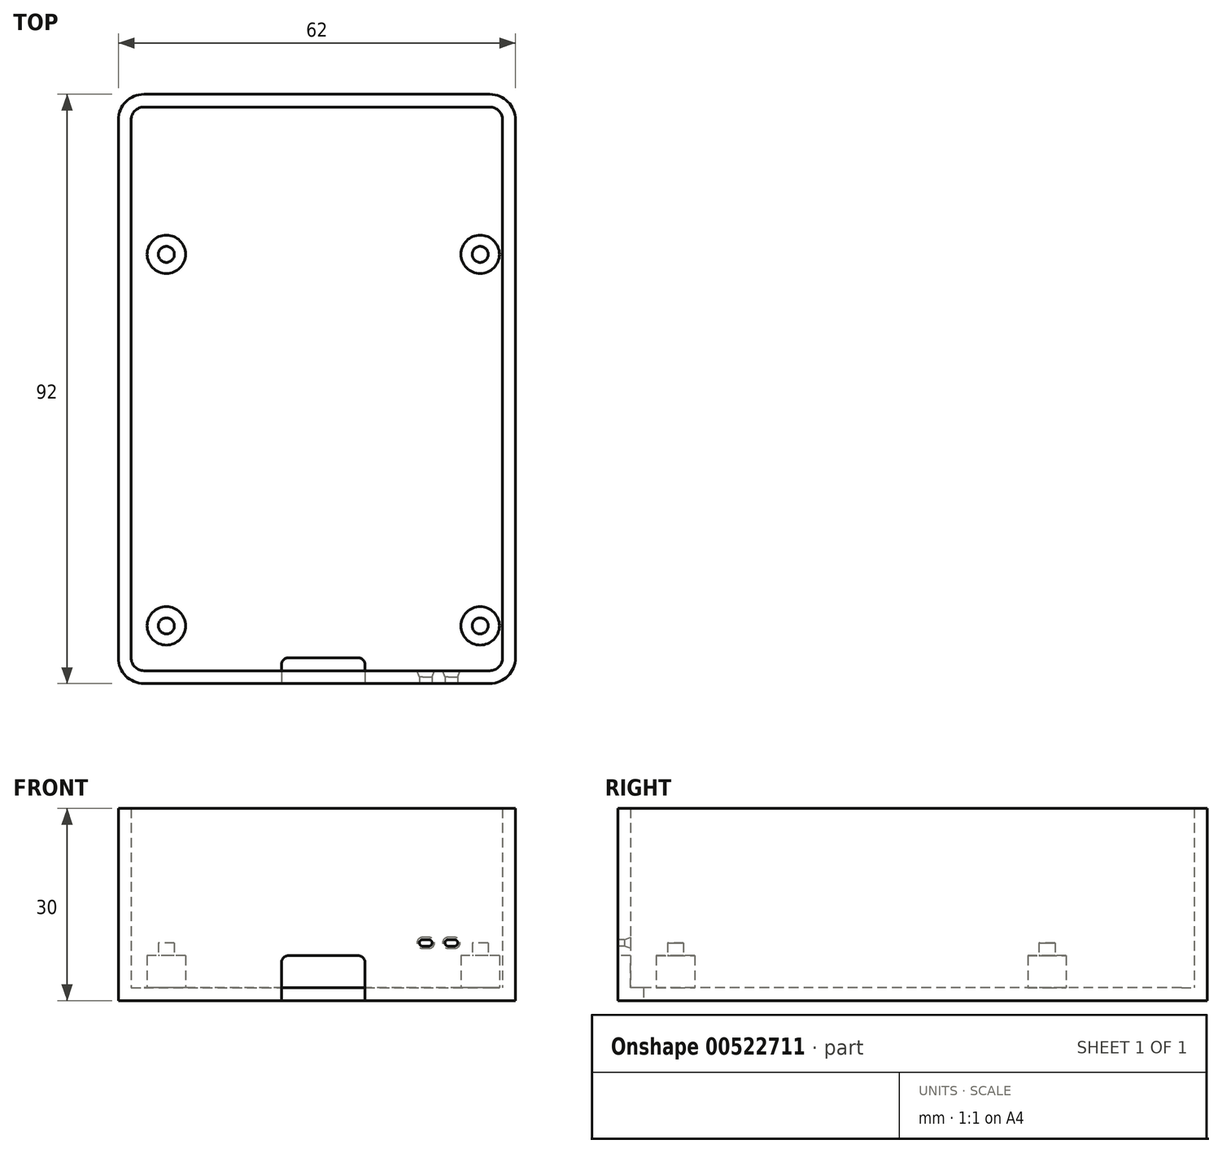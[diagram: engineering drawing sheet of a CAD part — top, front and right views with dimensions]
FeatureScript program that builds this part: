
annotation { "Feature Type Name" : "Feature", "Feature Type Description" : "" }
export const myFeature = defineFeature(function(context is Context, id is Id, definition is map)
    precondition{}
    {
        {
            var Q0;
            Q0=qCreatedBy(makeId("Top.planeOp"),FACE);
            var sketch = newSketch(context, id + "F0", { "sketchPlane" : qUnion([Q0])});
            skLineSegment(sketch, "E0.bottom", {"start": v(62, 0) * mm, "end": v(0, 0) * mm});
            skLineSegment(sketch, "E0.top", {"start": v(62, 92) * mm, "end": v(0, 92) * mm});
            skLineSegment(sketch, "E0.left", {"start": v(62, 0) * mm, "end": v(62, 92) * mm});
            skLineSegment(sketch, "E0.right", {"start": v(0, 0) * mm, "end": v(0, 92) * mm});
            skSolve(sketch);
        }
        {
            var Q0;
            Q0=makeQuery(id+"F0.imprint","IMPRINT",FACE,{"disambiguationData":[TD([[makeQuery(id+"F0.imprint","IMPRINT",EDGE,{"derivedFrom":sQuery(id+"F0.wireOp",EDGE,"E0.bottom")}),-1.0]])]});
            extrude(context, id + "F1", {"entities" : qUnion([Q0]), "depth" : 2 * mm});
        }
        {
            var Q0;
            Q0=makeQuery(id+"F1.opExtrude","CAP_FACE",FACE,{"disambiguationData":[OSD([sQuery(id+"F0.wireOp",EDGE,"E0.bottom"),sQuery(id+"F0.wireOp",EDGE,"E0.top"),sQuery(id+"F0.wireOp",EDGE,"E0.left"),sQuery(id+"F0.wireOp",EDGE,"E0.right")])],"isStart":false});
            var sketch = newSketch(context, id + "F2", { "sketchPlane" : qUnion([Q0])});
            skLineSegment(sketch, "E1.0", {"start": v(2, 2) * mm, "end": v(60, 2) * mm});
            skLineSegment(sketch, "E1.1", {"start": v(2, 90) * mm, "end": v(2, 2) * mm});
            skLineSegment(sketch, "E1.2", {"start": v(60, 90) * mm, "end": v(2, 90) * mm});
            skLineSegment(sketch, "E1.3", {"start": v(60, 2) * mm, "end": v(60, 90) * mm});
            skLineSegment(sketch, "E2.bottom", {"start": v(7.5, 67) * mm, "end": v(56.5, 67) * mm, "construction": true});
            skLineSegment(sketch, "E2.top", {"start": v(7.5, 9) * mm, "end": v(56.5, 9) * mm, "construction": true});
            skLineSegment(sketch, "E2.left", {"start": v(7.5, 67) * mm, "end": v(7.5, 9) * mm, "construction": true});
            skLineSegment(sketch, "E2.right", {"start": v(56.5, 67) * mm, "end": v(56.5, 9) * mm, "construction": true});
            skCircle(sketch, "E3", {"center": v(7.5, 67) * mm, "radius": 3 * mm});
            skCircle(sketch, "E4", {"center": v(56.5, 67) * mm, "radius": 3 * mm});
            skCircle(sketch, "E5", {"center": v(56.5, 9) * mm, "radius": 3 * mm});
            skCircle(sketch, "E6", {"center": v(7.5, 9) * mm, "radius": 3 * mm});
            skSolve(sketch);
        }
        {
            var Q0;
            Q0=makeQuery(id+"F2.imprint","IMPRINT",FACE,{"disambiguationData":[TD([[makeQuery(id+"F2.imprint","IMPRINT",EDGE,{"derivedFrom":sQuery(id+"F2.wireOp",EDGE,"E1.0")}),-1.0]])]});
            var Q1;
            Q1=makeQuery(id+"F2.imprint","IMPRINT",FACE,{"disambiguationData":[TD([[makeQuery(id+"F2.imprint","IMPRINT",EDGE,{"derivedFrom":sQuery(id+"F2.wireOp",EDGE,"E3")}),1.0]])]});
            var Q2;
            Q2=makeQuery(id+"F2.imprint","IMPRINT",FACE,{"disambiguationData":[TD([[makeQuery(id+"F2.imprint","IMPRINT",EDGE,{"derivedFrom":sQuery(id+"F2.wireOp",EDGE,"E4")}),1.0]])]});
            var Q3;
            Q3=makeQuery(id+"F2.imprint","IMPRINT",FACE,{"disambiguationData":[TD([[makeQuery(id+"F2.imprint","IMPRINT",EDGE,{"derivedFrom":sQuery(id+"F2.wireOp",EDGE,"E6")}),1.0]])]});
            var Q4;
            Q4=makeQuery(id+"F2.imprint","IMPRINT",FACE,{"disambiguationData":[TD([[makeQuery(id+"F2.imprint","IMPRINT",EDGE,{"derivedFrom":sQuery(id+"F2.wireOp",EDGE,"E5")}),1.0]])]});
            extrude(context, id + "F3", {"entities" : qUnion([Q0, Q1, Q2, Q3, Q4]), "operationType" : NewBodyOperationType.ADD, "depth" : 28 * mm});
        }
        {
            var Q0;
            Q0=makeQuery(id+"F3.opExtrude","CAP_FACE",FACE,{"disambiguationData":[OSD([sQuery(id+"F2.wireOp",EDGE,"E3")])],"isStart":false});
            var Q1;
            Q1=makeQuery(id+"F3.opExtrude","CAP_FACE",FACE,{"disambiguationData":[OSD([sQuery(id+"F2.wireOp",EDGE,"E4")])],"isStart":false});
            var Q2;
            Q2=makeQuery(id+"F3.opExtrude","CAP_FACE",FACE,{"disambiguationData":[OSD([sQuery(id+"F2.wireOp",EDGE,"E5")])],"isStart":false});
            var Q3;
            Q3=makeQuery(id+"F3.opExtrude","CAP_FACE",FACE,{"disambiguationData":[OSD([sQuery(id+"F2.wireOp",EDGE,"E6")])],"isStart":false});
            extrude(context, id + "F4", {"entities" : qUnion([Q0, Q1, Q2, Q3]), "operationType" : NewBodyOperationType.REMOVE, "oppositeDirection" : true, "depth" : 23 * mm, "offsetDistance" : 25.4 * mm});
        }
        {
            var Q0;
            Q0=makeQuery(id+"F4.boolean.opBoolean","COPY",FACE,{"derivedFrom":makeQuery(id+"F4.opExtrude","CAP_FACE",FACE,{"disambiguationData":[OSD([sQuery(id+"F2.wireOp",EDGE,"E6")])],"isStart":false})});
            var sketch = newSketch(context, id + "F5", { "sketchPlane" : qUnion([Q0])});
            skCircle(sketch, "E7", {"center": v(7.5, 9) * mm, "radius": 1.25 * mm});
            skSolve(sketch);
        }
        {
            var Q0;
            Q0=qSketchRegion(id+"F5",true);
            extrude(context, id + "F6", {"entities" : qUnion([Q0]), "operationType" : NewBodyOperationType.ADD, "depth" : 2 * mm});
        }
        {
            var Q0;
            Q0=makeQuery(id+"F4.boolean.opBoolean","COPY",FACE,{"derivedFrom":makeQuery(id+"F4.opExtrude","CAP_FACE",FACE,{"disambiguationData":[OSD([sQuery(id+"F2.wireOp",EDGE,"E5")])],"isStart":false})});
            var sketch = newSketch(context, id + "F7", { "sketchPlane" : qUnion([Q0])});
            skCircle(sketch, "E8", {"center": v(56.5, 9) * mm, "radius": 1.25 * mm});
            skSolve(sketch);
        }
        {
            var Q0;
            Q0=qSketchRegion(id+"F7",true);
            extrude(context, id + "F8", {"entities" : qUnion([Q0]), "operationType" : NewBodyOperationType.ADD, "depth" : 2 * mm});
        }
        {
            var Q0;
            Q0=makeQuery(id+"F4.boolean.opBoolean","COPY",FACE,{"derivedFrom":makeQuery(id+"F4.opExtrude","CAP_FACE",FACE,{"disambiguationData":[OSD([sQuery(id+"F2.wireOp",EDGE,"E4")])],"isStart":false})});
            var sketch = newSketch(context, id + "F9", { "sketchPlane" : qUnion([Q0])});
            skCircle(sketch, "E9", {"center": v(56.5, 67) * mm, "radius": 1.25 * mm});
            skSolve(sketch);
        }
        {
            var Q0;
            Q0=qSketchRegion(id+"F9",true);
            extrude(context, id + "F10", {"entities" : qUnion([Q0]), "operationType" : NewBodyOperationType.ADD, "depth" : 2 * mm, "offsetDistance" : 25.4 * mm});
        }
        {
            var Q0;
            Q0=makeQuery(id+"F4.boolean.opBoolean","COPY",FACE,{"derivedFrom":makeQuery(id+"F4.opExtrude","CAP_FACE",FACE,{"disambiguationData":[OSD([sQuery(id+"F2.wireOp",EDGE,"E3")])],"isStart":false})});
            var sketch = newSketch(context, id + "F11", { "sketchPlane" : qUnion([Q0])});
            skCircle(sketch, "E10", {"center": v(7.5, 67) * mm, "radius": 1.25 * mm});
            skSolve(sketch);
        }
        {
            var Q0;
            Q0=qSketchRegion(id+"F11",true);
            extrude(context, id + "F12", {"entities" : qUnion([Q0]), "operationType" : NewBodyOperationType.ADD, "depth" : 2 * mm});
        }
        {
            var Q0;
            {var subQ0=sQuery(id+"F0.wireOp",EDGE,"E0.bottom");Q0=makeQuery(id+"F3.boolean.opBoolean","MERGE",FACE,{"derivedFrom":[makeQuery(id+"F1.opExtrude","SWEPT_FACE",FACE,{"disambiguationData":[OSD([subQ0])]}),makeQuery(id+"F3.opExtrude","SWEPT_FACE",FACE,{"disambiguationData":[OSD([subQ0])]})]});}
            var sketch = newSketch(context, id + "F13", { "sketchPlane" : qUnion([Q0])});
            skLineSegment(sketch, "E11.bottom", {"start": v(51.5, 9.5) * mm, "end": v(52.5, 9.5) * mm});
            skLineSegment(sketch, "E11.top", {"start": v(51.5, 8.5) * mm, "end": v(52.5, 8.5) * mm});
            skLineSegment(sketch, "E11.left", {"start": v(51, 9) * mm, "end": v(51, 9) * mm});
            skLineSegment(sketch, "E11.right", {"start": v(53, 9) * mm, "end": v(53, 9) * mm});
            skLineSegment(sketch, "E12.bottom", {"start": v(47.5, 9.5) * mm, "end": v(48.5, 9.5) * mm});
            skLineSegment(sketch, "E12.top", {"start": v(47.5, 8.5) * mm, "end": v(48.5, 8.5) * mm});
            skLineSegment(sketch, "E12.left", {"start": v(47, 9) * mm, "end": v(47, 9) * mm});
            skLineSegment(sketch, "E12.right", {"start": v(49, 9) * mm, "end": v(49, 9) * mm});
            skLineSegment(sketch, "E13", {"start": v(56.5, 9.01) * mm, "end": v(56.5, 6.99) * mm, "construction": true});
            skLineSegment(sketch, "E14", {"start": v(52.63, 7) * mm, "end": v(33.92, 7) * mm, "construction": true});
            skLineSegment(sketch, "E15.bottom", {"start": v(37.5, 7) * mm, "end": v(26.5, 7) * mm});
            skLineSegment(sketch, "E15.top", {"start": v(38.5, 0) * mm, "end": v(25.5, 0) * mm});
            skLineSegment(sketch, "E15.left", {"start": v(38.5, 6) * mm, "end": v(38.5, 0) * mm});
            skLineSegment(sketch, "E15.right", {"start": v(25.5, 6) * mm, "end": v(25.5, 0) * mm});
            skPoint(sketch, "E16.visualSharp", {"position": v(25.5, 7) * mm});
            skArc(sketch, "E16.filletArc", {"start": v(26.5, 7) * mm, "mid": v(25.8, 6.7) * mm, "end": v(25.5, 6) * mm});
            skPoint(sketch, "E17.visualSharp", {"position": v(38.5, 7) * mm});
            skArc(sketch, "E17.filletArc", {"start": v(38.5, 6) * mm, "mid": v(38.2, 6.7) * mm, "end": v(37.5, 7) * mm});
            skPoint(sketch, "E18.visualSharp", {"position": v(47, 9.5) * mm});
            skArc(sketch, "E18.filletArc", {"start": v(47.5, 9.5) * mm, "mid": v(47.15, 9.35) * mm, "end": v(47, 9) * mm});
            skPoint(sketch, "E19.visualSharp", {"position": v(49, 9.5) * mm});
            skArc(sketch, "E19.filletArc", {"start": v(49, 9) * mm, "mid": v(48.85, 9.35) * mm, "end": v(48.5, 9.5) * mm});
            skPoint(sketch, "E20.visualSharp", {"position": v(49, 8.5) * mm});
            skArc(sketch, "E20.filletArc", {"start": v(48.5, 8.5) * mm, "mid": v(48.85, 8.65) * mm, "end": v(49, 9) * mm});
            skPoint(sketch, "E21.visualSharp", {"position": v(47, 8.5) * mm});
            skArc(sketch, "E21.filletArc", {"start": v(47, 9) * mm, "mid": v(47.15, 8.65) * mm, "end": v(47.5, 8.5) * mm});
            skPoint(sketch, "E22.visualSharp", {"position": v(51, 9.5) * mm});
            skArc(sketch, "E22.filletArc", {"start": v(51.5, 9.5) * mm, "mid": v(51.15, 9.35) * mm, "end": v(51, 9) * mm});
            skPoint(sketch, "E23.visualSharp", {"position": v(53, 9.5) * mm});
            skArc(sketch, "E23.filletArc", {"start": v(53, 9) * mm, "mid": v(52.85, 9.35) * mm, "end": v(52.5, 9.5) * mm});
            skPoint(sketch, "E24.visualSharp", {"position": v(53, 8.5) * mm});
            skArc(sketch, "E24.filletArc", {"start": v(52.5, 8.5) * mm, "mid": v(52.85, 8.65) * mm, "end": v(53, 9) * mm});
            skPoint(sketch, "E25.visualSharp", {"position": v(51, 8.5) * mm});
            skArc(sketch, "E25.filletArc", {"start": v(51, 9) * mm, "mid": v(51.15, 8.65) * mm, "end": v(51.5, 8.5) * mm});
            skSolve(sketch);
        }
        {
            var Q0;
            Q0=makeQuery(id+"F13.imprint","IMPRINT",FACE,{"disambiguationData":[TD([[makeQuery(id+"F13.imprint","IMPRINT",EDGE,{"derivedFrom":sQuery(id+"F13.wireOp",EDGE,"E15.bottom")}),1.0]])]});
            var Q1;
            Q1=makeQuery(id+"F13.imprint","IMPRINT",FACE,{"disambiguationData":[TD([[makeQuery(id+"F13.imprint","IMPRINT",EDGE,{"derivedFrom":sQuery(id+"F13.wireOp",EDGE,"E12.bottom")}),-1.0]])]});
            var Q2;
            Q2=makeQuery(id+"F13.imprint","IMPRINT",FACE,{"disambiguationData":[TD([[makeQuery(id+"F13.imprint","IMPRINT",EDGE,{"derivedFrom":sQuery(id+"F13.wireOp",EDGE,"E11.bottom")}),-1.0]])]});
            extrude(context, id + "F14", {"entities" : qUnion([Q0, Q1, Q2]), "operationType" : NewBodyOperationType.REMOVE, "oppositeDirection" : true, "depth" : 4 * mm});
        }
        {
            var Q0;
            Q0=makeQuery(id+"F14.boolean.opBoolean","COPY",EDGE,{"derivedFrom":makeQuery(id+"F14.opExtrude","CAP_EDGE",EDGE,{"disambiguationData":[OSD([sQuery(id+"F13.wireOp",EDGE,"E15.right")])],"isStart":false})});
            var Q1;
            Q1=makeQuery(id+"F14.boolean.opBoolean","COPY",EDGE,{"derivedFrom":makeQuery(id+"F14.opExtrude","CAP_EDGE",EDGE,{"disambiguationData":[OSD([sQuery(id+"F13.wireOp",EDGE,"E15.left")])],"isStart":false})});
            fillet(context, id + "F15", {"entities" : qUnion([Q0, Q1]), "radius" : 1 * mm, "tangentPropagation" : true, "allowEdgeOverflow" : false});
        }
        {
            var Q0;
            Q0=makeQuery(id+"F3.opExtrude","SWEPT_EDGE",EDGE,{"disambiguationData":[OSD([sQuery(id+"F2.wireOp",EDGE,"E1.1"),sQuery(id+"F2.wireOp",EDGE,"E1.2")])]});
            var Q1;
            Q1=makeQuery(id+"F3.opExtrude","SWEPT_EDGE",EDGE,{"disambiguationData":[OSD([sQuery(id+"F2.wireOp",EDGE,"E1.2"),sQuery(id+"F2.wireOp",EDGE,"E1.3")])]});
            var Q2;
            Q2=makeQuery(id+"F3.opExtrude","SWEPT_EDGE",EDGE,{"disambiguationData":[OSD([sQuery(id+"F2.wireOp",EDGE,"E1.0"),sQuery(id+"F2.wireOp",EDGE,"E1.3")])]});
            var Q3;
            Q3=makeQuery(id+"F3.opExtrude","SWEPT_EDGE",EDGE,{"disambiguationData":[OSD([sQuery(id+"F2.wireOp",EDGE,"E1.0"),sQuery(id+"F2.wireOp",EDGE,"E1.1")])]});
            fillet(context, id + "F16", {"entities" : qUnion([Q0, Q1, Q2, Q3]), "radius" : 2 * mm, "tangentPropagation" : true, "allowEdgeOverflow" : false});
        }
        {
            var Q0;
            {var subQ0=sQuery(id+"F0.wireOp",EDGE,"E0.right");var subQ1=sQuery(id+"F0.wireOp",EDGE,"E0.top");Q0=makeQuery(id+"F3.boolean.opBoolean","MERGE",EDGE,{"derivedFrom":[makeQuery(id+"F1.opExtrude","SWEPT_EDGE",EDGE,{"disambiguationData":[OSD([subQ1,subQ0])]}),makeQuery(id+"F3.opExtrude","SWEPT_EDGE",EDGE,{"disambiguationData":[OSD([subQ1,subQ0])]})]});}
            var Q1;
            {var subQ0=sQuery(id+"F0.wireOp",EDGE,"E0.left");var subQ1=sQuery(id+"F0.wireOp",EDGE,"E0.top");Q1=makeQuery(id+"F3.boolean.opBoolean","MERGE",EDGE,{"derivedFrom":[makeQuery(id+"F1.opExtrude","SWEPT_EDGE",EDGE,{"disambiguationData":[OSD([subQ1,subQ0])]}),makeQuery(id+"F3.opExtrude","SWEPT_EDGE",EDGE,{"disambiguationData":[OSD([subQ1,subQ0])]})]});}
            var Q2;
            {var subQ0=sQuery(id+"F0.wireOp",EDGE,"E0.left");var subQ1=sQuery(id+"F0.wireOp",EDGE,"E0.bottom");Q2=makeQuery(id+"F3.boolean.opBoolean","MERGE",EDGE,{"derivedFrom":[makeQuery(id+"F1.opExtrude","SWEPT_EDGE",EDGE,{"disambiguationData":[OSD([subQ1,subQ0])]}),makeQuery(id+"F3.opExtrude","SWEPT_EDGE",EDGE,{"disambiguationData":[OSD([subQ1,subQ0])]})]});}
            var Q3;
            {var subQ0=sQuery(id+"F0.wireOp",EDGE,"E0.right");var subQ1=sQuery(id+"F0.wireOp",EDGE,"E0.bottom");Q3=makeQuery(id+"F3.boolean.opBoolean","MERGE",EDGE,{"derivedFrom":[makeQuery(id+"F1.opExtrude","SWEPT_EDGE",EDGE,{"disambiguationData":[OSD([subQ1,subQ0])]}),makeQuery(id+"F3.opExtrude","SWEPT_EDGE",EDGE,{"disambiguationData":[OSD([subQ1,subQ0])]})]});}
            fillet(context, id + "F17", {"entities" : qUnion([Q0, Q1, Q2, Q3]), "radius" : 4 * mm, "tangentPropagation" : true, "allowEdgeOverflow" : false});
        }
        {
            var Q0;
            Q0=makeQuery(id+"F14.boolean.opBoolean","INTERSECT",EDGE,{"derivedFrom":[makeQuery(id+"F3.opExtrude","SWEPT_FACE",FACE,{"disambiguationData":[OSD([sQuery(id+"F2.wireOp",EDGE,"E1.0")])]}),makeQuery(id+"F14.opExtrude","SWEPT_FACE",FACE,{"disambiguationData":[OSD([sQuery(id+"F13.wireOp",EDGE,"E22.filletArc"),sQuery(id+"F13.wireOp",EDGE,"E25.filletArc")])]})]});
            var Q1;
            Q1=makeQuery(id+"F14.boolean.opBoolean","INTERSECT",EDGE,{"derivedFrom":[makeQuery(id+"F3.opExtrude","SWEPT_FACE",FACE,{"disambiguationData":[OSD([sQuery(id+"F2.wireOp",EDGE,"E1.0")])]}),makeQuery(id+"F14.opExtrude","SWEPT_FACE",FACE,{"disambiguationData":[OSD([sQuery(id+"F13.wireOp",EDGE,"E18.filletArc"),sQuery(id+"F13.wireOp",EDGE,"E21.filletArc")])]})]});
            chamfer(context, id + "F18", {"entities" : qUnion([Q0, Q1]), "chamferType" : ChamferType.OFFSET_ANGLE, "width" : 1 * mm, "oppositeDirection" : false, "angle" : 20 * degree, "tangentPropagation" : true});
        }
    });
